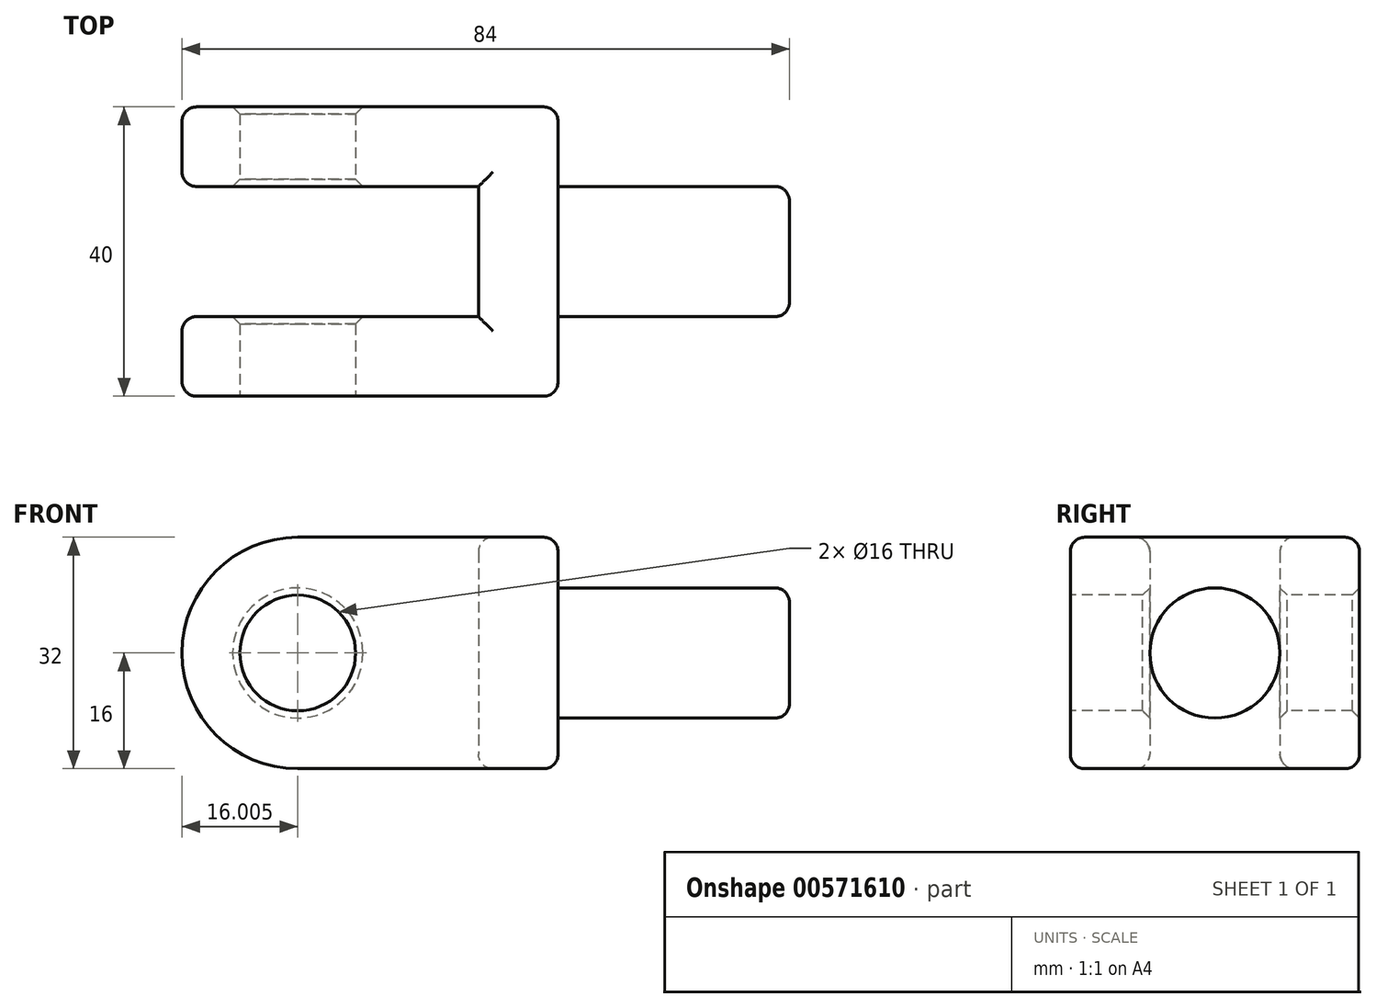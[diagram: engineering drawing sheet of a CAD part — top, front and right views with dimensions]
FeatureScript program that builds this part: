
annotation { "Feature Type Name" : "Feature", "Feature Type Description" : "" }
export const myFeature = defineFeature(function(context is Context, id is Id, definition is map)
    precondition{}
    {
        {
            var Q0;
            Q0=qCreatedBy(makeId("Front.planeOp"),FACE);
            var sketch = newSketch(context, id + "F0", { "sketchPlane" : qUnion([Q0])});
            skLineSegment(sketch, "E0", {"start": v(0, -56.18) * mm, "end": v(0, 37.47) * mm, "construction": true});
            skLineSegment(sketch, "E1", {"start": v(-60.47, 0) * mm, "end": v(78.3, 0) * mm, "construction": true});
            skLineSegment(sketch, "E2", {"start": v(22.62, 16) * mm, "end": v(22.62, -16) * mm});
            skLineSegment(sketch, "E3", {"start": v(22.62, -16) * mm, "end": v(-13.38, -16) * mm});
            skLineSegment(sketch, "E4", {"start": v(22.62, 16) * mm, "end": v(-13.38, 16) * mm});
            skArc(sketch, "E5", {"start": v(-13.38, -16) * mm, "mid": v(-29.38, 0) * mm, "end": v(-13.38, 16) * mm});
            skSolve(sketch);
        }
        {
            var Q0;
            Q0=qSketchRegion(id+"F0",true);
            extrude(context, id + "F1", {"entities" : qUnion([Q0]), "depth" : 20 * mm, "offsetDistance" : 25 * mm, "hasSecondDirection" : true, "secondDirectionOppositeDirection" : true, "secondDirectionDepth" : 20 * mm});
        }
        {
            var Q0;
            Q0=makeQuery(id+"F1.opExtrude","CAP_FACE",FACE,{"disambiguationData":[OSD([sQuery(id+"F0.wireOp",EDGE,"E2"),sQuery(id+"F0.wireOp",EDGE,"E3"),sQuery(id+"F0.wireOp",EDGE,"E4"),sQuery(id+"F0.wireOp",EDGE,"E5")])],"isStart":false});
            var sketch = newSketch(context, id + "F2", { "sketchPlane" : qUnion([Q0])});
            skCircle(sketch, "E6", {"center": v(-13.38, 0) * mm, "radius": 8 * mm});
            skSolve(sketch);
        }
        {
            var Q0;
            Q0=qSketchRegion(id+"F2",true);
            extrude(context, id + "F3", {"entities" : qUnion([Q0]), "operationType" : NewBodyOperationType.REMOVE, "endBound" : BoundingType.THROUGH_ALL, "oppositeDirection" : true, "depth" : 25 * mm, "offsetDistance" : 25 * mm});
        }
        {
            var Q0;
            Q0=qCreatedBy(makeId("Top.planeOp"),FACE);
            var sketch = newSketch(context, id + "F4", { "sketchPlane" : qUnion([Q0])});
            skPoint(sketch, "E7.middle", {"position": v(0, 0) * mm});
            skLineSegment(sketch, "E8.bottom", {"start": v(11.62, -9) * mm, "end": v(-50.92, -9) * mm});
            skLineSegment(sketch, "E8.top", {"start": v(11.62, 9) * mm, "end": v(-50.92, 9) * mm});
            skLineSegment(sketch, "E8.left", {"start": v(11.62, -9) * mm, "end": v(11.62, 9) * mm});
            skLineSegment(sketch, "E8.right", {"start": v(-50.92, -9) * mm, "end": v(-50.92, 9) * mm});
            skSolve(sketch);
        }
        {
            var Q0;
            Q0=qSketchRegion(id+"F4",true);
            extrude(context, id + "F5", {"entities" : qUnion([Q0]), "operationType" : NewBodyOperationType.REMOVE, "endBound" : BoundingType.THROUGH_ALL, "depth" : 25 * mm, "offsetDistance" : 25 * mm, "hasSecondDirection" : true, "secondDirectionOppositeDirection" : true, "secondDirectionDepth" : 25 * mm});
        }
        {
            var Q0;
            Q0=makeQuery(id+"F1.opExtrude","SWEPT_FACE",FACE,{"disambiguationData":[OSD([sQuery(id+"F0.wireOp",EDGE,"E2")])]});
            var sketch = newSketch(context, id + "F6", { "sketchPlane" : qUnion([Q0])});
            skCircle(sketch, "E9", {"center": v(0, 0) * mm, "radius": 9 * mm});
            skSolve(sketch);
        }
        {
            var Q0;
            Q0=qSketchRegion(id+"F6",true);
            extrude(context, id + "F7", {"entities" : qUnion([Q0]), "operationType" : NewBodyOperationType.ADD, "depth" : 32 * mm, "offsetDistance" : 25 * mm});
        }
        {
            var Q0;
            Q0=makeQuery(id+"F3.boolean.opBoolean","COPY",EDGE,{"derivedFrom":makeQuery(id+"F3.opExtrude","CAP_EDGE",EDGE,{"disambiguationData":[OSD([sQuery(id+"F2.wireOp",EDGE,"E6")])],"isStart":true})});
            var Q1;
            Q1=makeQuery(id+"F3.boolean.opBoolean","INTERSECT",EDGE,{"derivedFrom":[makeQuery(id+"F1.opExtrude","CAP_FACE",FACE,{"disambiguationData":[OSD([sQuery(id+"F0.wireOp",EDGE,"E2"),sQuery(id+"F0.wireOp",EDGE,"E3"),sQuery(id+"F0.wireOp",EDGE,"E4"),sQuery(id+"F0.wireOp",EDGE,"E5")])],"isStart":true}),makeQuery(id+"F3.opExtrude","SWEPT_FACE",FACE,{"disambiguationData":[OSD([sQuery(id+"F2.wireOp",EDGE,"E6")])]})]});
            var Q2;
            Q2=makeQuery(id+"F5.boolean.opBoolean","INTERSECT",EDGE,{"derivedFrom":[makeQuery(id+"F3.boolean.opBoolean","COPY",FACE,{"derivedFrom":makeQuery(id+"F3.opExtrude","SWEPT_FACE",FACE,{"disambiguationData":[OSD([sQuery(id+"F2.wireOp",EDGE,"E6")])]})}),makeQuery(id+"F5.opExtrude","SWEPT_FACE",FACE,{"disambiguationData":[OSD([sQuery(id+"F4.wireOp",EDGE,"E8.bottom")])]})]});
            var Q3;
            Q3=makeQuery(id+"F5.boolean.opBoolean","INTERSECT",EDGE,{"derivedFrom":[makeQuery(id+"F3.boolean.opBoolean","COPY",FACE,{"derivedFrom":makeQuery(id+"F3.opExtrude","SWEPT_FACE",FACE,{"disambiguationData":[OSD([sQuery(id+"F2.wireOp",EDGE,"E6")])]})}),makeQuery(id+"F5.opExtrude","SWEPT_FACE",FACE,{"disambiguationData":[OSD([sQuery(id+"F4.wireOp",EDGE,"E8.top")])]})]});
            chamfer(context, id + "F8", {"entities" : qUnion([Q0, Q1, Q2, Q3]), "width" : 1 * mm, "tangentPropagation" : true});
        }
        {
            var Q0;
            Q0=makeQuery(id+"F1.opExtrude","CAP_EDGE",EDGE,{"disambiguationData":[OSD([sQuery(id+"F0.wireOp",EDGE,"E5")])],"isStart":false});
            var Q1;
            Q1=makeQuery(id+"F5.boolean.opBoolean","INTERSECT",EDGE,{"derivedFrom":[makeQuery(id+"F1.opExtrude","SWEPT_FACE",FACE,{"disambiguationData":[OSD([sQuery(id+"F0.wireOp",EDGE,"E4")])]}),makeQuery(id+"F5.opExtrude","SWEPT_FACE",FACE,{"disambiguationData":[OSD([sQuery(id+"F4.wireOp",EDGE,"E8.bottom")])]})]});
            var Q2;
            Q2=makeQuery(id+"F5.boolean.opBoolean","INTERSECT",EDGE,{"derivedFrom":[makeQuery(id+"F1.opExtrude","SWEPT_FACE",FACE,{"disambiguationData":[OSD([sQuery(id+"F0.wireOp",EDGE,"E4")])]}),makeQuery(id+"F5.opExtrude","SWEPT_FACE",FACE,{"disambiguationData":[OSD([sQuery(id+"F4.wireOp",EDGE,"E8.left")])]})]});
            var Q3;
            Q3=makeQuery(id+"F5.boolean.opBoolean","INTERSECT",EDGE,{"derivedFrom":[makeQuery(id+"F1.opExtrude","SWEPT_FACE",FACE,{"disambiguationData":[OSD([sQuery(id+"F0.wireOp",EDGE,"E3")])]}),makeQuery(id+"F5.opExtrude","SWEPT_FACE",FACE,{"disambiguationData":[OSD([sQuery(id+"F4.wireOp",EDGE,"E8.left")])]})]});
            var Q4;
            Q4=makeQuery(id+"F5.boolean.opBoolean","INTERSECT",EDGE,{"derivedFrom":[makeQuery(id+"F1.opExtrude","SWEPT_FACE",FACE,{"disambiguationData":[OSD([sQuery(id+"F0.wireOp",EDGE,"E3")])]}),makeQuery(id+"F5.opExtrude","SWEPT_FACE",FACE,{"disambiguationData":[OSD([sQuery(id+"F4.wireOp",EDGE,"E8.top")])]})]});
            var Q5;
            Q5=makeQuery(id+"F1.opExtrude","CAP_EDGE",EDGE,{"disambiguationData":[OSD([sQuery(id+"F0.wireOp",EDGE,"E5")])],"isStart":true});
            var Q6;
            Q6=makeQuery(id+"F1.opExtrude","CAP_EDGE",EDGE,{"disambiguationData":[OSD([sQuery(id+"F0.wireOp",EDGE,"E2")])],"isStart":true});
            var Q7;
            Q7=makeQuery(id+"F1.opExtrude","SWEPT_EDGE",EDGE,{"disambiguationData":[OSD([sQuery(id+"F0.wireOp",EDGE,"E2"),sQuery(id+"F0.wireOp",EDGE,"E4")])]});
            var Q8;
            Q8=makeQuery(id+"F1.opExtrude","CAP_EDGE",EDGE,{"disambiguationData":[OSD([sQuery(id+"F0.wireOp",EDGE,"E2")])],"isStart":false});
            var Q9;
            Q9=makeQuery(id+"F1.opExtrude","SWEPT_EDGE",EDGE,{"disambiguationData":[OSD([sQuery(id+"F0.wireOp",EDGE,"E2"),sQuery(id+"F0.wireOp",EDGE,"E3")])]});
            var Q10;
            Q10=makeQuery(id+"F7.opExtrude","CAP_EDGE",EDGE,{"disambiguationData":[OSD([sQuery(id+"F6.wireOp",EDGE,"E9")])],"isStart":false});
            var Q11;
            Q11=makeQuery(id+"F7.opExtrude","CAP_EDGE",EDGE,{"disambiguationData":[OSD([sQuery(id+"F6.wireOp",EDGE,"E9")])],"isStart":true});
            fillet(context, id + "F9", {"entities" : qUnion([Q0, Q1, Q2, Q3, Q4, Q5, Q6, Q7, Q8, Q9, Q10, Q11]), "radius" : 2 * mm, "tangentPropagation" : true, "allowEdgeOverflow" : false});
        }
    });
